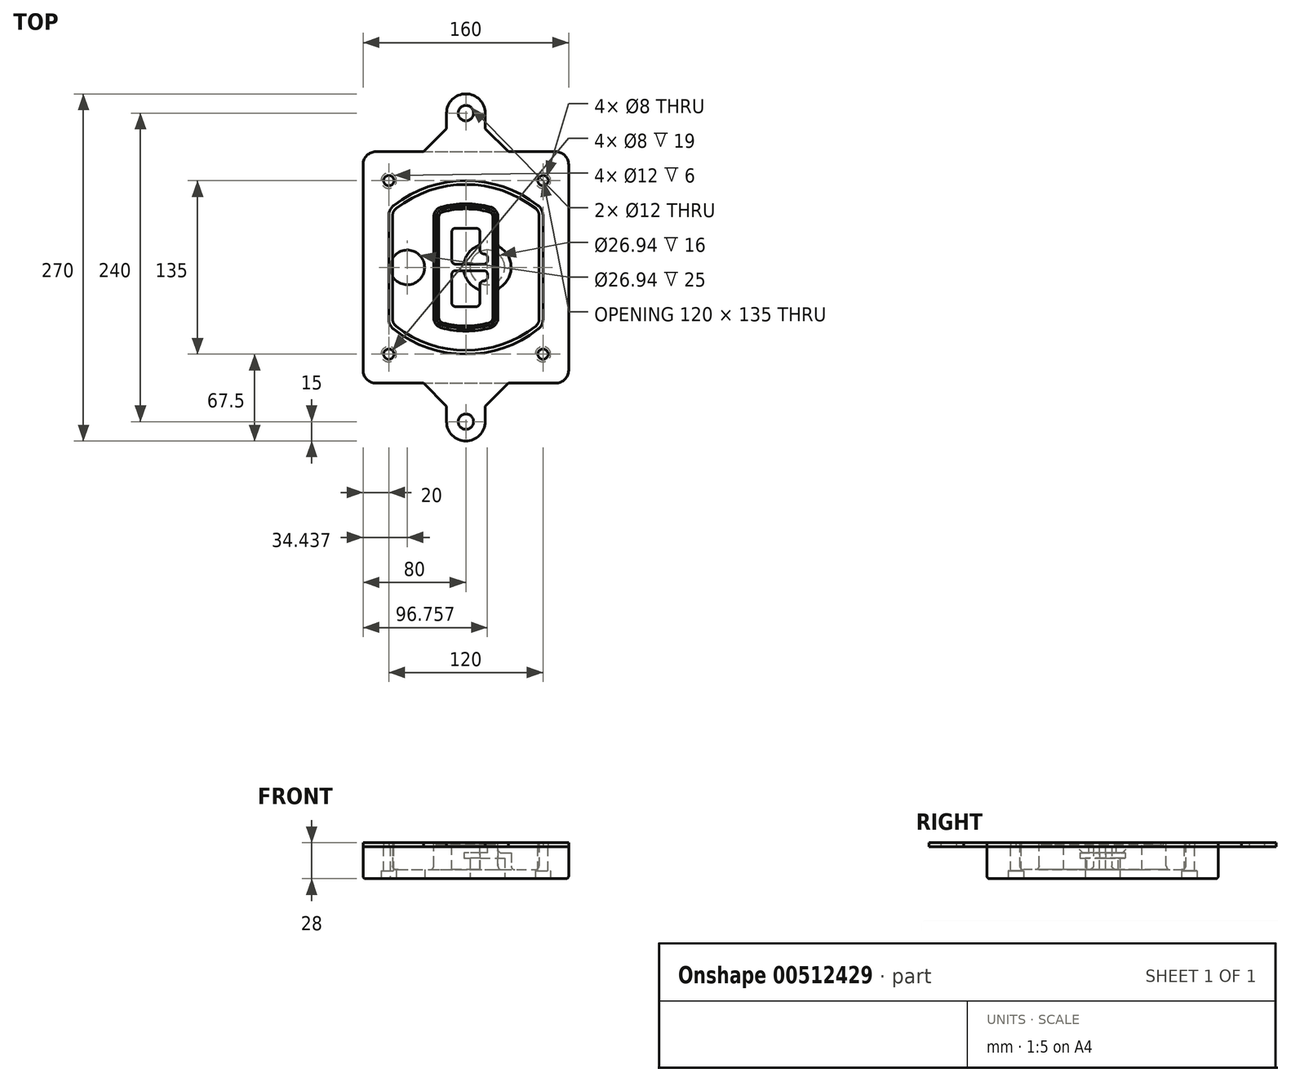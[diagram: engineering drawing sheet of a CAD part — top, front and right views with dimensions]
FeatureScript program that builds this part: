
annotation { "Feature Type Name" : "Feature", "Feature Type Description" : "" }
export const myFeature = defineFeature(function(context is Context, id is Id, definition is map)
    precondition{}
    {
        {
            var Q0;
            Q0=qCreatedBy(makeId("Top.planeOp"),FACE);
            var sketch = newSketch(context, id + "F0", { "sketchPlane" : qUnion([Q0])});
            skPoint(sketch, "E0.rect.middle", {"position": v(0, 0) * mm});
            skLineSegment(sketch, "E1.bottom", {"start": v(-70, -90) * mm, "end": v(70, -90) * mm});
            skLineSegment(sketch, "E1.top", {"start": v(-70, 90) * mm, "end": v(70, 90) * mm});
            skLineSegment(sketch, "E1.left", {"start": v(-80, -80) * mm, "end": v(-80, 80) * mm});
            skLineSegment(sketch, "E1.right", {"start": v(80, -80) * mm, "end": v(80, 80) * mm});
            skLineSegment(sketch, "E2", {"start": v(-80, 90) * mm, "end": v(80, -90) * mm, "construction": true});
            skLineSegment(sketch, "E3", {"start": v(80, 90) * mm, "end": v(-80, -90) * mm, "construction": true});
            skCircle(sketch, "E4", {"center": v(-60, 67.5) * mm, "radius": 4 * mm});
            skCircle(sketch, "E5", {"center": v(60, 67.5) * mm, "radius": 4 * mm});
            skCircle(sketch, "E6", {"center": v(60, -67.5) * mm, "radius": 4 * mm});
            skCircle(sketch, "E7", {"center": v(-60, -67.5) * mm, "radius": 4 * mm});
            skLineSegment(sketch, "E8", {"start": v(-60, 67.5) * mm, "end": v(60, 67.5) * mm, "construction": true});
            skLineSegment(sketch, "E9", {"start": v(60, 67.5) * mm, "end": v(60, -67.5) * mm, "construction": true});
            skLineSegment(sketch, "E10", {"start": v(60, -67.5) * mm, "end": v(-60, -67.5) * mm, "construction": true});
            skLineSegment(sketch, "E11", {"start": v(-60, -67.5) * mm, "end": v(-60, 67.5) * mm, "construction": true});
            skLineSegment(sketch, "E12", {"start": v(-60, 40.3) * mm, "end": v(-60, -40.3) * mm});
            skLineSegment(sketch, "E13", {"start": v(60, 40.3) * mm, "end": v(60, -40.3) * mm});
            skArc(sketch, "E14", {"start": v(56.15, 48.18) * mm, "mid": v(0, 67.5) * mm, "end": v(-56.15, 48.18) * mm});
            skArc(sketch, "E15", {"start": v(-56.15, -48.18) * mm, "mid": v(0, -67.5) * mm, "end": v(56.15, -48.18) * mm});
            skLineSegment(sketch, "E16", {"start": v(-60, 0) * mm, "end": v(60, 0) * mm, "construction": true});
            skPoint(sketch, "E17.visualSharp", {"position": v(-60, -45) * mm});
            skArc(sketch, "E17.filletArc", {"start": v(-60, -40.3) * mm, "mid": v(-58.99, -44.68) * mm, "end": v(-56.15, -48.18) * mm});
            skPoint(sketch, "E18.visualSharp", {"position": v(-60, 45) * mm});
            skArc(sketch, "E18.filletArc", {"start": v(-56.15, 48.18) * mm, "mid": v(-58.99, 44.68) * mm, "end": v(-60, 40.3) * mm});
            skPoint(sketch, "E19.visualSharp", {"position": v(60, 45) * mm});
            skArc(sketch, "E19.filletArc", {"start": v(60, 40.3) * mm, "mid": v(58.99, 44.68) * mm, "end": v(56.15, 48.18) * mm});
            skPoint(sketch, "E20.visualSharp", {"position": v(60, -45) * mm});
            skArc(sketch, "E20.filletArc", {"start": v(56.15, -48.18) * mm, "mid": v(58.99, -44.68) * mm, "end": v(60, -40.3) * mm});
            skPoint(sketch, "E21.visualSharp", {"position": v(-80, 90) * mm});
            skArc(sketch, "E21.filletArc", {"start": v(-70, 90) * mm, "mid": v(-77.07, 87.07) * mm, "end": v(-80, 80) * mm});
            skPoint(sketch, "E22.visualSharp", {"position": v(80, 90) * mm});
            skArc(sketch, "E22.filletArc", {"start": v(80, 80) * mm, "mid": v(77.07, 87.07) * mm, "end": v(70, 90) * mm});
            skPoint(sketch, "E23.visualSharp", {"position": v(80, -90) * mm});
            skArc(sketch, "E23.filletArc", {"start": v(70, -90) * mm, "mid": v(77.07, -87.07) * mm, "end": v(80, -80) * mm});
            skPoint(sketch, "E24.visualSharp", {"position": v(-80, -90) * mm});
            skArc(sketch, "E24.filletArc", {"start": v(-80, -80) * mm, "mid": v(-77.07, -87.07) * mm, "end": v(-70, -90) * mm});
            skArc(sketch, "E25.0", {"start": v(57, 40.3) * mm, "mid": v(56.3, 43.36) * mm, "end": v(54.3, 45.81) * mm});
            skLineSegment(sketch, "E25.1", {"start": v(57, 40.3) * mm, "end": v(57, -40.3) * mm});
            skArc(sketch, "E25.2", {"start": v(54.3, -45.81) * mm, "mid": v(56.3, -43.36) * mm, "end": v(57, -40.3) * mm});
            skArc(sketch, "E25.3", {"start": v(-54.3, -45.81) * mm, "mid": v(0, -64.5) * mm, "end": v(54.3, -45.81) * mm});
            skArc(sketch, "E25.4", {"start": v(-57, -40.3) * mm, "mid": v(-56.3, -43.36) * mm, "end": v(-54.3, -45.81) * mm});
            skArc(sketch, "E25.5", {"start": v(54.3, 45.81) * mm, "mid": v(0, 64.5) * mm, "end": v(-54.3, 45.81) * mm});
            skLineSegment(sketch, "E25.6", {"start": v(-57, 40.3) * mm, "end": v(-57, -40.3) * mm});
            skArc(sketch, "E25.7", {"start": v(-54.3, 45.81) * mm, "mid": v(-56.3, 43.36) * mm, "end": v(-57, 40.3) * mm});
            skArc(sketch, "E26.0", {"start": v(-58.62, 51.33) * mm, "mid": v(-62.58, 46.43) * mm, "end": v(-64, 40.3) * mm});
            skArc(sketch, "E26.1", {"start": v(58.62, 51.33) * mm, "mid": v(0, 71.5) * mm, "end": v(-58.62, 51.33) * mm});
            skArc(sketch, "E26.2", {"start": v(64, 40.3) * mm, "mid": v(62.58, 46.43) * mm, "end": v(58.62, 51.33) * mm});
            skLineSegment(sketch, "E26.3", {"start": v(64, 40.3) * mm, "end": v(64, -40.3) * mm});
            skArc(sketch, "E26.4", {"start": v(58.62, -51.33) * mm, "mid": v(62.58, -46.43) * mm, "end": v(64, -40.3) * mm});
            skLineSegment(sketch, "E26.5", {"start": v(-64, 40.3) * mm, "end": v(-64, -40.3) * mm});
            skArc(sketch, "E26.6", {"start": v(-58.62, -51.33) * mm, "mid": v(0, -71.5) * mm, "end": v(58.62, -51.33) * mm});
            skArc(sketch, "E26.7", {"start": v(-64, -40.3) * mm, "mid": v(-62.58, -46.43) * mm, "end": v(-58.62, -51.33) * mm});
            skSolve(sketch);
        }
        {
            var Q0;
            Q0=makeQuery(id+"F0.imprint","IMPRINT",FACE,{"disambiguationData":[TD([[makeQuery(id+"F0.imprint","IMPRINT",EDGE,{"derivedFrom":sQuery(id+"F0.wireOp",EDGE,"E1.bottom")}),1.0]])]});
            var Q1;
            Q1=makeQuery(id+"F0.imprint","IMPRINT",FACE,{"disambiguationData":[TD([[makeQuery(id+"F0.imprint","IMPRINT",EDGE,{"derivedFrom":sQuery(id+"F0.wireOp",EDGE,"E12")}),1.0]])]});
            var Q2;
            Q2=makeQuery(id+"F0.imprint","IMPRINT",FACE,{"disambiguationData":[TD([[makeQuery(id+"F0.imprint","IMPRINT",EDGE,{"derivedFrom":sQuery(id+"F0.wireOp",EDGE,"E25.0")}),1.0]])]});
            var Q3;
            Q3=makeQuery(id+"F0.imprint","IMPRINT",FACE,{"disambiguationData":[TD([[makeQuery(id+"F0.imprint","IMPRINT",EDGE,{"derivedFrom":sQuery(id+"F0.wireOp",EDGE,"E12")}),-1.0]])]});
            extrude(context, id + "F1", {"entities" : qUnion([Q0, Q1, Q2, Q3]), "oppositeDirection" : true, "depth" : 25 * mm});
        }
        {
            var Q0;
            Q0=makeQuery(id+"F0.imprint","IMPRINT",FACE,{"disambiguationData":[TD([[makeQuery(id+"F0.imprint","IMPRINT",EDGE,{"derivedFrom":sQuery(id+"F0.wireOp",EDGE,"E12")}),1.0]])]});
            extrude(context, id + "F2", {"entities" : qUnion([Q0]), "operationType" : NewBodyOperationType.ADD, "depth" : 3 * mm});
        }
        {
            var Q0;
            Q0=makeQuery(id+"F0.imprint","IMPRINT",FACE,{"disambiguationData":[TD([[makeQuery(id+"F0.imprint","IMPRINT",EDGE,{"derivedFrom":sQuery(id+"F0.wireOp",EDGE,"E25.0")}),1.0]])]});
            extrude(context, id + "F3", {"entities" : qUnion([Q0]), "operationType" : NewBodyOperationType.REMOVE, "oppositeDirection" : true, "depth" : 18 * mm});
        }
        {
            var Q0;
            Q0=makeQuery(id+"F2.opExtrude","CAP_FACE",FACE,{"disambiguationData":[OSD([sQuery(id+"F0.wireOp",EDGE,"E12"),sQuery(id+"F0.wireOp",EDGE,"E13"),sQuery(id+"F0.wireOp",EDGE,"E14"),sQuery(id+"F0.wireOp",EDGE,"E15"),sQuery(id+"F0.wireOp",EDGE,"E17.filletArc"),sQuery(id+"F0.wireOp",EDGE,"E18.filletArc"),sQuery(id+"F0.wireOp",EDGE,"E19.filletArc"),sQuery(id+"F0.wireOp",EDGE,"E20.filletArc"),sQuery(id+"F0.wireOp",EDGE,"E25.0"),sQuery(id+"F0.wireOp",EDGE,"E25.1"),sQuery(id+"F0.wireOp",EDGE,"E25.2"),sQuery(id+"F0.wireOp",EDGE,"E25.3"),sQuery(id+"F0.wireOp",EDGE,"E25.4"),sQuery(id+"F0.wireOp",EDGE,"E25.5"),sQuery(id+"F0.wireOp",EDGE,"E25.6"),sQuery(id+"F0.wireOp",EDGE,"E25.7")])],"isStart":false});
            var sketch = newSketch(context, id + "F4", { "sketchPlane" : qUnion([Q0])});
            skArc(sketch, "E27.0", {"start": v(-19.08, -46.97) * mm, "mid": v(0, -49.5) * mm, "end": v(19.08, -46.97) * mm});
            skArc(sketch, "E28.0", {"start": v(19.08, 46.97) * mm, "mid": v(0, 49.5) * mm, "end": v(-19.08, 46.97) * mm});
            skLineSegment(sketch, "E29", {"start": v(-25, 39.25) * mm, "end": v(-25, -39.25) * mm});
            skLineSegment(sketch, "E30", {"start": v(25, 39.25) * mm, "end": v(25, -39.25) * mm});
            skLineSegment(sketch, "E31", {"start": v(-25, 45.1) * mm, "end": v(25, 45.1) * mm, "construction": true});
            skLineSegment(sketch, "E32", {"start": v(-25, -45.1) * mm, "end": v(25, -45.1) * mm, "construction": true});
            skPoint(sketch, "E33.visualSharp", {"position": v(-25, 45.1) * mm});
            skArc(sketch, "E33.filletArc", {"start": v(-19.08, 46.97) * mm, "mid": v(-23.35, 44.11) * mm, "end": v(-25, 39.25) * mm});
            skPoint(sketch, "E34.visualSharp", {"position": v(25, 45.1) * mm});
            skArc(sketch, "E34.filletArc", {"start": v(25, 39.25) * mm, "mid": v(23.35, 44.11) * mm, "end": v(19.08, 46.97) * mm});
            skPoint(sketch, "E35.visualSharp", {"position": v(25, -45.1) * mm});
            skArc(sketch, "E35.filletArc", {"start": v(19.08, -46.97) * mm, "mid": v(23.35, -44.11) * mm, "end": v(25, -39.25) * mm});
            skPoint(sketch, "E36.visualSharp", {"position": v(-25, -45.1) * mm});
            skArc(sketch, "E36.filletArc", {"start": v(-25, -39.25) * mm, "mid": v(-23.35, -44.11) * mm, "end": v(-19.08, -46.97) * mm});
            skArc(sketch, "E37.0", {"start": v(54.3, 45.81) * mm, "mid": v(0, 64.5) * mm, "end": v(-54.3, 45.81) * mm});
            skArc(sketch, "E37.1", {"start": v(-54.3, 45.81) * mm, "mid": v(-56.3, 43.36) * mm, "end": v(-57, 40.3) * mm});
            skLineSegment(sketch, "E37.2", {"start": v(-57, 40.3) * mm, "end": v(-57, -40.3) * mm});
            skArc(sketch, "E37.3", {"start": v(-57, -40.3) * mm, "mid": v(-56.3, -43.36) * mm, "end": v(-54.3, -45.81) * mm});
            skArc(sketch, "E37.4", {"start": v(-54.3, -45.81) * mm, "mid": v(0, -64.5) * mm, "end": v(54.3, -45.81) * mm});
            skArc(sketch, "E37.5", {"start": v(54.3, -45.81) * mm, "mid": v(56.3, -43.36) * mm, "end": v(57, -40.3) * mm});
            skLineSegment(sketch, "E37.6", {"start": v(57, 40.3) * mm, "end": v(57, -40.3) * mm});
            skArc(sketch, "E37.7", {"start": v(57, 40.3) * mm, "mid": v(56.3, 43.36) * mm, "end": v(54.3, 45.81) * mm});
            skLineSegment(sketch, "E38.0", {"start": v(23, 39.25) * mm, "end": v(23, -39.25) * mm});
            skArc(sketch, "E38.1", {"start": v(18.56, -45.04) * mm, "mid": v(21.76, -42.9) * mm, "end": v(23, -39.25) * mm});
            skArc(sketch, "E38.2", {"start": v(-18.56, -45.04) * mm, "mid": v(0, -47.5) * mm, "end": v(18.56, -45.04) * mm});
            skArc(sketch, "E38.3", {"start": v(-23, -39.25) * mm, "mid": v(-21.76, -42.9) * mm, "end": v(-18.56, -45.04) * mm});
            skLineSegment(sketch, "E38.4", {"start": v(-23, 39.25) * mm, "end": v(-23, -39.25) * mm});
            skArc(sketch, "E38.5", {"start": v(23, 39.25) * mm, "mid": v(21.76, 42.9) * mm, "end": v(18.56, 45.04) * mm});
            skArc(sketch, "E38.6", {"start": v(-18.56, 45.04) * mm, "mid": v(-21.76, 42.9) * mm, "end": v(-23, 39.25) * mm});
            skArc(sketch, "E38.7", {"start": v(18.56, 45.04) * mm, "mid": v(0, 47.5) * mm, "end": v(-18.56, 45.04) * mm});
            skArc(sketch, "E39.0", {"start": v(21, 39.25) * mm, "mid": v(20.18, 41.68) * mm, "end": v(18.04, 43.1) * mm});
            skLineSegment(sketch, "E39.1", {"start": v(21, 39.25) * mm, "end": v(21, -39.25) * mm});
            skArc(sketch, "E39.2", {"start": v(18.04, -43.1) * mm, "mid": v(20.18, -41.68) * mm, "end": v(21, -39.25) * mm});
            skArc(sketch, "E39.3", {"start": v(-18.04, -43.1) * mm, "mid": v(0, -45.5) * mm, "end": v(18.04, -43.1) * mm});
            skArc(sketch, "E39.4", {"start": v(-21, -39.25) * mm, "mid": v(-20.18, -41.68) * mm, "end": v(-18.04, -43.1) * mm});
            skArc(sketch, "E39.5", {"start": v(18.04, 43.1) * mm, "mid": v(0, 45.5) * mm, "end": v(-18.04, 43.1) * mm});
            skLineSegment(sketch, "E39.6", {"start": v(-21, 39.25) * mm, "end": v(-21, -39.25) * mm});
            skArc(sketch, "E39.7", {"start": v(-18.04, 43.1) * mm, "mid": v(-20.18, 41.68) * mm, "end": v(-21, 39.25) * mm});
            skLineSegment(sketch, "E40", {"start": v(-25, 0) * mm, "end": v(25, 0) * mm, "construction": true});
            skLineSegment(sketch, "E41", {"start": v(-11, 5.5) * mm, "end": v(-11, 27.5) * mm});
            skLineSegment(sketch, "E42", {"start": v(-8, 30.5) * mm, "end": v(8, 30.5) * mm});
            skLineSegment(sketch, "E43", {"start": v(11, 27.5) * mm, "end": v(11, 13.5) * mm});
            skLineSegment(sketch, "E44", {"start": v(14, 10.5) * mm, "end": v(14, 10.5) * mm});
            skLineSegment(sketch, "E45", {"start": v(17, 7.5) * mm, "end": v(17, 5.5) * mm});
            skLineSegment(sketch, "E46", {"start": v(14, 2.5) * mm, "end": v(-8, 2.5) * mm});
            skPoint(sketch, "E47.visualSharp", {"position": v(-11, 30.5) * mm});
            skArc(sketch, "E47.filletArc", {"start": v(-8, 30.5) * mm, "mid": v(-10.12, 29.62) * mm, "end": v(-11, 27.5) * mm});
            skPoint(sketch, "E48.visualSharp", {"position": v(11, 30.5) * mm});
            skArc(sketch, "E48.filletArc", {"start": v(11, 27.5) * mm, "mid": v(10.12, 29.62) * mm, "end": v(8, 30.5) * mm});
            skPoint(sketch, "E49.visualSharp", {"position": v(11, 10.5) * mm});
            skArc(sketch, "E49.filletArc", {"start": v(11, 13.5) * mm, "mid": v(11.88, 11.38) * mm, "end": v(14, 10.5) * mm});
            skPoint(sketch, "E50.visualSharp", {"position": v(17, 10.5) * mm});
            skArc(sketch, "E50.filletArc", {"start": v(17, 7.5) * mm, "mid": v(16.12, 9.62) * mm, "end": v(14, 10.5) * mm});
            skPoint(sketch, "E51.visualSharp", {"position": v(17, 2.5) * mm});
            skArc(sketch, "E51.filletArc", {"start": v(14, 2.5) * mm, "mid": v(16.12, 3.38) * mm, "end": v(17, 5.5) * mm});
            skPoint(sketch, "E52.visualSharp", {"position": v(-11, 2.5) * mm});
            skArc(sketch, "E52.filletArc", {"start": v(-11, 5.5) * mm, "mid": v(-10.12, 3.38) * mm, "end": v(-8, 2.5) * mm});
            skLineSegment(sketch, "E53.0.MirrorCS", {"start": v(14, -2.5) * mm, "end": v(-8, -2.5) * mm});
            skArc(sketch, "E54.0.MirrorCS", {"start": v(-11, -5.5) * mm, "mid": v(-10.12, -3.38) * mm, "end": v(-8, -2.5) * mm});
            skLineSegment(sketch, "E55.0.MirrorCS", {"start": v(-11, -5.5) * mm, "end": v(-11, -27.5) * mm});
            skArc(sketch, "E56.0.MirrorCS", {"start": v(-8, -30.5) * mm, "mid": v(-10.12, -29.62) * mm, "end": v(-11, -27.5) * mm});
            skLineSegment(sketch, "E57.0.MirrorCS", {"start": v(-8, -30.5) * mm, "end": v(8, -30.5) * mm});
            skArc(sketch, "E58.0.MirrorCS", {"start": v(11, -27.5) * mm, "mid": v(10.12, -29.62) * mm, "end": v(8, -30.5) * mm});
            skLineSegment(sketch, "E59.0.MirrorCS", {"start": v(11, -27.5) * mm, "end": v(11, -13.5) * mm});
            skArc(sketch, "E60.0.MirrorCS", {"start": v(11, -13.5) * mm, "mid": v(11.88, -11.38) * mm, "end": v(14, -10.5) * mm});
            skArc(sketch, "E61.0.MirrorCS", {"start": v(17, -7.5) * mm, "mid": v(16.12, -9.62) * mm, "end": v(14, -10.5) * mm});
            skLineSegment(sketch, "E62.0.MirrorCS", {"start": v(17, -7.5) * mm, "end": v(17, -5.5) * mm});
            skArc(sketch, "E63.0.MirrorCS", {"start": v(14, -2.5) * mm, "mid": v(16.12, -3.38) * mm, "end": v(17, -5.5) * mm});
            skSolve(sketch);
        }
        {
            var Q0;
            Q0=makeQuery(id+"F4.imprint","IMPRINT",FACE,{"disambiguationData":[TD([[makeQuery(id+"F4.imprint","IMPRINT",EDGE,{"derivedFrom":sQuery(id+"F4.wireOp",EDGE,"E27.0")}),1.0]])]});
            var Q1;
            Q1=makeQuery(id+"F4.imprint","IMPRINT",FACE,{"disambiguationData":[TD([[makeQuery(id+"F4.imprint","IMPRINT",EDGE,{"derivedFrom":sQuery(id+"F4.wireOp",EDGE,"E38.0")}),-1.0]])]});
            var Q2;
            Q2=makeQuery(id+"F4.imprint","IMPRINT",FACE,{"disambiguationData":[TD([[makeQuery(id+"F4.imprint","IMPRINT",EDGE,{"derivedFrom":sQuery(id+"F4.wireOp",EDGE,"E39.0")}),1.0]])]});
            extrude(context, id + "F5", {"entities" : qUnion([Q0, Q1, Q2]), "operationType" : NewBodyOperationType.ADD, "endBound" : BoundingType.UP_TO_NEXT, "oppositeDirection" : true, "depth" : 25 * mm});
        }
        {
            var Q0;
            Q0=makeQuery(id+"F4.imprint","IMPRINT",FACE,{"disambiguationData":[TD([[makeQuery(id+"F4.imprint","IMPRINT",EDGE,{"derivedFrom":sQuery(id+"F4.wireOp",EDGE,"E38.0")}),-1.0]])]});
            extrude(context, id + "F6", {"entities" : qUnion([Q0]), "operationType" : NewBodyOperationType.REMOVE, "oppositeDirection" : true, "depth" : 2 * mm});
        }
        {
            var Q0;
            Q0=makeQuery(id+"F1.opExtrude","CAP_FACE",FACE,{"disambiguationData":[OSD([sQuery(id+"F0.wireOp",EDGE,"E1.bottom"),sQuery(id+"F0.wireOp",EDGE,"E1.top"),sQuery(id+"F0.wireOp",EDGE,"E1.left"),sQuery(id+"F0.wireOp",EDGE,"E1.right"),sQuery(id+"F0.wireOp",EDGE,"E4"),sQuery(id+"F0.wireOp",EDGE,"E5"),sQuery(id+"F0.wireOp",EDGE,"E6"),sQuery(id+"F0.wireOp",EDGE,"E7"),sQuery(id+"F0.wireOp",EDGE,"E21.filletArc"),sQuery(id+"F0.wireOp",EDGE,"E22.filletArc"),sQuery(id+"F0.wireOp",EDGE,"E23.filletArc"),sQuery(id+"F0.wireOp",EDGE,"E24.filletArc")])],"isStart":false});
            var sketch = newSketch(context, id + "F7", { "sketchPlane" : qUnion([Q0])});
            skCircle(sketch, "E64", {"center": v(16.76, 0) * mm, "radius": 13.47 * mm});
            skCircle(sketch, "E65", {"center": v(-45.56, 0) * mm, "radius": 13.47 * mm});
            skLineSegment(sketch, "E66", {"start": v(80, 0) * mm, "end": v(-80, 0) * mm});
            skCircle(sketch, "E67", {"center": v(16.76, 0) * mm, "radius": 18.47 * mm});
            skCircle(sketch, "E68", {"center": v(60, -67.5) * mm, "radius": 6 * mm});
            skCircle(sketch, "E69", {"center": v(-60, -67.5) * mm, "radius": 6 * mm});
            skCircle(sketch, "E70", {"center": v(-60, 67.5) * mm, "radius": 6 * mm});
            skCircle(sketch, "E71", {"center": v(60, 67.5) * mm, "radius": 6 * mm});
            skSolve(sketch);
        }
        {
            var Q0;
            {var subQ1=sQuery(id+"F7.wireOp",EDGE,"E66");var subQ4=sQuery(id+"F7.wireOp",EDGE,"E64");var subQ6=makeQuery(id+"F7.imprint","INTERSECT",VERTEX,{"disambiguationData":[OD(0.0)],"derivedFrom":[subQ4,subQ1]});Q0=makeQuery(id+"F7.imprint","IMPRINT",FACE,{"disambiguationData":[TD([[makeQuery(id+"F7.imprint","IMPRINT",EDGE,{"disambiguationData":[TD([[subQ6,-1.0]])],"derivedFrom":subQ4}),-1.0]])]});}
            var Q1;
            {var subQ0=sQuery(id+"F7.wireOp",EDGE,"E66");var subQ1=sQuery(id+"F7.wireOp",EDGE,"E64");var subQ3=makeQuery(id+"F7.imprint","INTERSECT",VERTEX,{"disambiguationData":[OD(0.0)],"derivedFrom":[subQ1,subQ0]});Q1=makeQuery(id+"F7.imprint","IMPRINT",FACE,{"disambiguationData":[TD([[makeQuery(id+"F7.imprint","IMPRINT",EDGE,{"disambiguationData":[TD([[subQ3,-1.0]])],"derivedFrom":subQ1}),1.0]])]});}
            var Q2;
            {var subQ0=sQuery(id+"F7.wireOp",EDGE,"E66");var subQ1=sQuery(id+"F7.wireOp",EDGE,"E64");var subQ3=makeQuery(id+"F7.imprint","INTERSECT",VERTEX,{"disambiguationData":[OD(0.0)],"derivedFrom":[subQ1,subQ0]});Q2=makeQuery(id+"F7.imprint","IMPRINT",FACE,{"disambiguationData":[TD([[makeQuery(id+"F7.imprint","IMPRINT",EDGE,{"disambiguationData":[TD([[subQ3,1.0]])],"derivedFrom":subQ1}),1.0]])]});}
            var Q3;
            {var subQ1=sQuery(id+"F7.wireOp",EDGE,"E66");var subQ4=sQuery(id+"F7.wireOp",EDGE,"E64");var subQ6=makeQuery(id+"F7.imprint","INTERSECT",VERTEX,{"disambiguationData":[OD(0.0)],"derivedFrom":[subQ4,subQ1]});Q3=makeQuery(id+"F7.imprint","IMPRINT",FACE,{"disambiguationData":[TD([[makeQuery(id+"F7.imprint","IMPRINT",EDGE,{"disambiguationData":[TD([[subQ6,1.0]])],"derivedFrom":subQ4}),-1.0]])]});}
            extrude(context, id + "F8", {"entities" : qUnion([Q0, Q1, Q2, Q3]), "operationType" : NewBodyOperationType.ADD, "oppositeDirection" : true, "depth" : 20 * mm});
        }
        {
            var Q0;
            {var subQ0=sQuery(id+"F7.wireOp",EDGE,"E66");var subQ1=sQuery(id+"F7.wireOp",EDGE,"E64");var subQ3=makeQuery(id+"F7.imprint","INTERSECT",VERTEX,{"disambiguationData":[OD(0.0)],"derivedFrom":[subQ1,subQ0]});Q0=makeQuery(id+"F7.imprint","IMPRINT",FACE,{"disambiguationData":[TD([[makeQuery(id+"F7.imprint","IMPRINT",EDGE,{"disambiguationData":[TD([[subQ3,-1.0]])],"derivedFrom":subQ1}),1.0]])]});}
            var Q1;
            {var subQ0=sQuery(id+"F7.wireOp",EDGE,"E66");var subQ1=sQuery(id+"F7.wireOp",EDGE,"E64");var subQ3=makeQuery(id+"F7.imprint","INTERSECT",VERTEX,{"disambiguationData":[OD(0.0)],"derivedFrom":[subQ1,subQ0]});Q1=makeQuery(id+"F7.imprint","IMPRINT",FACE,{"disambiguationData":[TD([[makeQuery(id+"F7.imprint","IMPRINT",EDGE,{"disambiguationData":[TD([[subQ3,1.0]])],"derivedFrom":subQ1}),1.0]])]});}
            extrude(context, id + "F9", {"entities" : qUnion([Q0, Q1]), "operationType" : NewBodyOperationType.REMOVE, "oppositeDirection" : true, "depth" : 16 * mm});
        }
        {
            var Q0;
            {var subQ0=sQuery(id+"F7.wireOp",EDGE,"E66");var subQ1=sQuery(id+"F7.wireOp",EDGE,"E65");var subQ3=makeQuery(id+"F7.imprint","INTERSECT",VERTEX,{"disambiguationData":[OD(0.0)],"derivedFrom":[subQ1,subQ0]});Q0=makeQuery(id+"F7.imprint","IMPRINT",FACE,{"disambiguationData":[TD([[makeQuery(id+"F7.imprint","IMPRINT",EDGE,{"disambiguationData":[TD([[subQ3,-1.0]])],"derivedFrom":subQ1}),1.0]])]});}
            var Q1;
            {var subQ0=sQuery(id+"F7.wireOp",EDGE,"E66");var subQ1=sQuery(id+"F7.wireOp",EDGE,"E65");var subQ3=makeQuery(id+"F7.imprint","INTERSECT",VERTEX,{"disambiguationData":[OD(0.0)],"derivedFrom":[subQ1,subQ0]});Q1=makeQuery(id+"F7.imprint","IMPRINT",FACE,{"disambiguationData":[TD([[makeQuery(id+"F7.imprint","IMPRINT",EDGE,{"disambiguationData":[TD([[subQ3,1.0]])],"derivedFrom":subQ1}),1.0]])]});}
            extrude(context, id + "F10", {"entities" : qUnion([Q0, Q1]), "operationType" : NewBodyOperationType.REMOVE, "oppositeDirection" : true, "depth" : 25 * mm});
        }
        {
            var Q0;
            Q0=makeQuery(id+"F7.imprint","IMPRINT",FACE,{"disambiguationData":[TD([[makeQuery(id+"F7.imprint","IMPRINT",EDGE,{"derivedFrom":sQuery(id+"F7.wireOp",EDGE,"E68")}),1.0]])]});
            var Q1;
            Q1=makeQuery(id+"F7.imprint","IMPRINT",FACE,{"disambiguationData":[TD([[makeQuery(id+"F7.imprint","IMPRINT",EDGE,{"derivedFrom":makeQuery(id+"F1.opExtrude","CAP_EDGE",EDGE,{"disambiguationData":[OSD([sQuery(id+"F0.wireOp",EDGE,"E5")])],"isStart":false})}),-1.0]])]});
            var Q2;
            Q2=makeQuery(id+"F7.imprint","IMPRINT",FACE,{"disambiguationData":[TD([[makeQuery(id+"F7.imprint","IMPRINT",EDGE,{"derivedFrom":sQuery(id+"F7.wireOp",EDGE,"E69")}),1.0]])]});
            var Q3;
            Q3=makeQuery(id+"F7.imprint","IMPRINT",FACE,{"disambiguationData":[TD([[makeQuery(id+"F7.imprint","IMPRINT",EDGE,{"derivedFrom":makeQuery(id+"F1.opExtrude","CAP_EDGE",EDGE,{"disambiguationData":[OSD([sQuery(id+"F0.wireOp",EDGE,"E4")])],"isStart":false})}),-1.0]])]});
            var Q4;
            Q4=makeQuery(id+"F7.imprint","IMPRINT",FACE,{"disambiguationData":[TD([[makeQuery(id+"F7.imprint","IMPRINT",EDGE,{"derivedFrom":sQuery(id+"F7.wireOp",EDGE,"E70")}),1.0]])]});
            var Q5;
            Q5=makeQuery(id+"F7.imprint","IMPRINT",FACE,{"disambiguationData":[TD([[makeQuery(id+"F7.imprint","IMPRINT",EDGE,{"derivedFrom":makeQuery(id+"F1.opExtrude","CAP_EDGE",EDGE,{"disambiguationData":[OSD([sQuery(id+"F0.wireOp",EDGE,"E7")])],"isStart":false})}),-1.0]])]});
            var Q6;
            Q6=makeQuery(id+"F7.imprint","IMPRINT",FACE,{"disambiguationData":[TD([[makeQuery(id+"F7.imprint","IMPRINT",EDGE,{"derivedFrom":sQuery(id+"F7.wireOp",EDGE,"E71")}),1.0]])]});
            var Q7;
            Q7=makeQuery(id+"F7.imprint","IMPRINT",FACE,{"disambiguationData":[TD([[makeQuery(id+"F7.imprint","IMPRINT",EDGE,{"derivedFrom":makeQuery(id+"F1.opExtrude","CAP_EDGE",EDGE,{"disambiguationData":[OSD([sQuery(id+"F0.wireOp",EDGE,"E6")])],"isStart":false})}),-1.0]])]});
            extrude(context, id + "F11", {"entities" : qUnion([Q0, Q1, Q2, Q3, Q4, Q5, Q6, Q7]), "operationType" : NewBodyOperationType.REMOVE, "oppositeDirection" : true, "depth" : 6 * mm});
        }
        {
            var Q0;
            Q0=makeQuery(id+"F9.boolean.opBoolean","COPY",FACE,{"derivedFrom":makeQuery(id+"F9.opExtrude","CAP_FACE",FACE,{"disambiguationData":[OSD([sQuery(id+"F7.wireOp",EDGE,"E64")])],"isStart":false})});
            var sketch = newSketch(context, id + "F12", { "sketchPlane" : qUnion([Q0])});
            skArc(sketch, "E72.0", {"start": v(11, 17.55) * mm, "mid": v(2.57, 11.82) * mm, "end": v(-1.54, 2.5) * mm});
            skArc(sketch, "E72.1", {"start": v(-1.54, -2.5) * mm, "mid": v(2.57, -11.82) * mm, "end": v(11, -17.55) * mm});
            skLineSegment(sketch, "E73", {"start": v(-1.54, -2.5) * mm, "end": v(14, -2.5) * mm});
            skLineSegment(sketch, "E74.0", {"start": v(14, 2.5) * mm, "end": v(-1.54, 2.5) * mm});
            skArc(sketch, "E74.1", {"start": v(14, 2.5) * mm, "mid": v(16.12, 3.38) * mm, "end": v(17, 5.5) * mm});
            skLineSegment(sketch, "E74.2", {"start": v(17, 7.5) * mm, "end": v(17, 5.5) * mm});
            skArc(sketch, "E74.3", {"start": v(17, 7.5) * mm, "mid": v(16.12, 9.62) * mm, "end": v(14, 10.5) * mm});
            skArc(sketch, "E74.4", {"start": v(11, 13.5) * mm, "mid": v(11.88, 11.38) * mm, "end": v(14, 10.5) * mm});
            skLineSegment(sketch, "E74.5", {"start": v(11, 17.55) * mm, "end": v(11, 13.5) * mm});
            skLineSegment(sketch, "E74.7", {"start": v(14, -2.5) * mm, "end": v(-1.54, -2.5) * mm});
            skArc(sketch, "E74.8", {"start": v(14, -2.5) * mm, "mid": v(16.12, -3.38) * mm, "end": v(17, -5.5) * mm});
            skLineSegment(sketch, "E74.9", {"start": v(17, -7.5) * mm, "end": v(17, -5.5) * mm});
            skArc(sketch, "E74.10", {"start": v(17, -7.5) * mm, "mid": v(16.12, -9.62) * mm, "end": v(14, -10.5) * mm});
            skArc(sketch, "E74.11", {"start": v(11, -13.5) * mm, "mid": v(11.88, -11.38) * mm, "end": v(14, -10.5) * mm});
            skLineSegment(sketch, "E74.12", {"start": v(11, -17.55) * mm, "end": v(11, -13.5) * mm});
            skPoint(sketch, "E75.orphan", {"position": v(11, -27.5) * mm});
            skPoint(sketch, "E76.orphan", {"position": v(-8, -2.5) * mm});
            skPoint(sketch, "E77.orphan", {"position": v(-8, 2.5) * mm});
            skPoint(sketch, "E78.orphan", {"position": v(11, 27.5) * mm});
            skSolve(sketch);
        }
        {
            var Q0;
            {var subQ7=sQuery(id+"F12.wireOp",EDGE,"E72.0");var subQ14=sQuery(id+"F12.wireOp",EDGE,"E72.1");var subQ16=sQuery(id+"F12.wireOp",EDGE,"E74.1");var subQ18=sQuery(id+"F12.wireOp",EDGE,"E74.8");Q0=qUnion([makeQuery(id+"F12.imprint","IMPRINT",FACE,{"disambiguationData":[TD([[makeQuery(id+"F12.imprint","IMPRINT",EDGE,{"derivedFrom":subQ7}),1.0]])]}),makeQuery(id+"F12.imprint","IMPRINT",FACE,{"disambiguationData":[TD([[makeQuery(id+"F12.imprint","IMPRINT",EDGE,{"derivedFrom":subQ14}),1.0]])]}),makeQuery(id+"F12.imprint","IMPRINT",FACE,{"disambiguationData":[TD([[makeQuery(id+"F12.imprint","IMPRINT",EDGE,{"derivedFrom":subQ16}),1.0]])]}),makeQuery(id+"F12.imprint","IMPRINT",FACE,{"disambiguationData":[TD([[makeQuery(id+"F12.imprint","IMPRINT",EDGE,{"derivedFrom":subQ18}),-1.0]])]})]);}
            var Q1;
            Q1=makeQuery(id+"F5.boolean.opBoolean","SPLIT",FACE,{"disambiguationData":[TD([makeQuery(id+"F5.opExtrude","SWEPT_FACE",FACE,{"disambiguationData":[OSD([sQuery(id+"F4.wireOp",EDGE,"E41")])]})])],"derivedFrom":makeQuery(id+"F3.boolean.opBoolean","COPY",FACE,{"derivedFrom":makeQuery(id+"F3.opExtrude","CAP_FACE",FACE,{"disambiguationData":[OSD([sQuery(id+"F0.wireOp",EDGE,"E25.0"),sQuery(id+"F0.wireOp",EDGE,"E25.1"),sQuery(id+"F0.wireOp",EDGE,"E25.2"),sQuery(id+"F0.wireOp",EDGE,"E25.3"),sQuery(id+"F0.wireOp",EDGE,"E25.4"),sQuery(id+"F0.wireOp",EDGE,"E25.5"),sQuery(id+"F0.wireOp",EDGE,"E25.6"),sQuery(id+"F0.wireOp",EDGE,"E25.7")])],"isStart":false})})});
            extrude(context, id + "F13", {"entities" : qUnion([Q0]), "operationType" : NewBodyOperationType.REMOVE, "endBound" : BoundingType.UP_TO_SURFACE, "endBoundEntityFace" : qUnion([Q1]), "depth" : 25 * mm});
        }
        {
            var Q0;
            Q0=makeQuery(id+"F3.boolean.opBoolean","COPY",EDGE,{"derivedFrom":makeQuery(id+"F3.opExtrude","CAP_EDGE",EDGE,{"disambiguationData":[OSD([sQuery(id+"F0.wireOp",EDGE,"E25.6")])],"isStart":false})});
            var Q1;
            Q1=makeQuery(id+"F8.boolean.opBoolean","INTERSECT",EDGE,{"derivedFrom":[makeQuery(id+"F5.opExtrude","SWEPT_FACE",FACE,{"disambiguationData":[OSD([sQuery(id+"F4.wireOp",EDGE,"E30")])]}),makeQuery(id+"F8.opExtrude","CAP_FACE",FACE,{"disambiguationData":[OSD([sQuery(id+"F7.wireOp",EDGE,"E67")])],"isStart":false})]});
            var Q2;
            Q2=makeQuery(id+"F8.boolean.opBoolean","INTERSECT",EDGE,{"disambiguationData":[OD(1.0)],"derivedFrom":[makeQuery(id+"F5.opExtrude","SWEPT_FACE",FACE,{"disambiguationData":[OSD([sQuery(id+"F4.wireOp",EDGE,"E30")])]}),makeQuery(id+"F8.opExtrude","SWEPT_FACE",FACE,{"disambiguationData":[OSD([sQuery(id+"F7.wireOp",EDGE,"E67")])]})]});
            var Q3;
            {var subQ0=sQuery(id+"F4.wireOp",EDGE,"E30");Q3=makeQuery(id+"F8.boolean.opBoolean","SPLIT",EDGE,{"disambiguationData":[TD([makeQuery(id+"F5.opExtrude","SWEPT_FACE",FACE,{"disambiguationData":[OSD([sQuery(id+"F4.wireOp",EDGE,"E35.filletArc")])]})])],"derivedFrom":makeQuery(id+"F5.opExtrude","CAP_EDGE",EDGE,{"disambiguationData":[OSD([subQ0])],"isStart":false})});}
            var Q4;
            {var subQ0=sQuery(id+"F0.wireOp",EDGE,"E25.7");var subQ1=sQuery(id+"F0.wireOp",EDGE,"E25.1");var subQ2=sQuery(id+"F0.wireOp",EDGE,"E25.6");var subQ3=sQuery(id+"F0.wireOp",EDGE,"E25.5");var subQ4=sQuery(id+"F0.wireOp",EDGE,"E25.4");var subQ5=sQuery(id+"F0.wireOp",EDGE,"E25.0");var subQ6=sQuery(id+"F0.wireOp",EDGE,"E25.2");var subQ7=sQuery(id+"F0.wireOp",EDGE,"E25.3");Q4=makeQuery(id+"F8.boolean.opBoolean","INTERSECT",EDGE,{"derivedFrom":[makeQuery(id+"F5.boolean.opBoolean","SPLIT",FACE,{"disambiguationData":[TD([makeQuery(id+"F2.opExtrude","SWEPT_FACE",FACE,{"disambiguationData":[OSD([subQ5])]})])],"derivedFrom":makeQuery(id+"F3.boolean.opBoolean","COPY",FACE,{"derivedFrom":makeQuery(id+"F3.opExtrude","CAP_FACE",FACE,{"disambiguationData":[OSD([subQ5,subQ1,subQ6,subQ7,subQ4,subQ3,subQ2,subQ0])],"isStart":false})})}),makeQuery(id+"F8.opExtrude","SWEPT_FACE",FACE,{"disambiguationData":[OSD([sQuery(id+"F7.wireOp",EDGE,"E67")])]})]});}
            var Q5;
            Q5=makeQuery(id+"F8.boolean.opBoolean","INTERSECT",EDGE,{"disambiguationData":[OD(0.0)],"derivedFrom":[makeQuery(id+"F5.opExtrude","SWEPT_FACE",FACE,{"disambiguationData":[OSD([sQuery(id+"F4.wireOp",EDGE,"E30")])]}),makeQuery(id+"F8.opExtrude","SWEPT_FACE",FACE,{"disambiguationData":[OSD([sQuery(id+"F7.wireOp",EDGE,"E67")])]})]});
            fillet(context, id + "F14", {"entities" : qUnion([Q0, Q1, Q2, Q3, Q4, Q5]), "radius" : 3 * mm, "tangentPropagation" : true, "allowEdgeOverflow" : false});
        }
        {
            var Q0;
            Q0=makeQuery(id+"F1.opExtrude","CAP_EDGE",EDGE,{"disambiguationData":[OSD([sQuery(id+"F0.wireOp",EDGE,"E1.bottom")])],"isStart":false});
            fillet(context, id + "F15", {"entities" : qUnion([Q0]), "radius" : 2 * mm, "tangentPropagation" : true, "allowEdgeOverflow" : false});
        }
        {
            var Q0;
            {var subQ0=sQuery(id+"F0.wireOp",EDGE,"E21.filletArc");var subQ1=sQuery(id+"F0.wireOp",EDGE,"E7");var subQ2=sQuery(id+"F0.wireOp",EDGE,"E6");var subQ3=sQuery(id+"F0.wireOp",EDGE,"E5");var subQ4=sQuery(id+"F0.wireOp",EDGE,"E4");var subQ5=sQuery(id+"F0.wireOp",EDGE,"E22.filletArc");var subQ6=sQuery(id+"F0.wireOp",EDGE,"E1.bottom");var subQ7=sQuery(id+"F0.wireOp",EDGE,"E1.right");var subQ8=sQuery(id+"F0.wireOp",EDGE,"E1.top");var subQ9=sQuery(id+"F0.wireOp",EDGE,"E1.left");var subQ10=sQuery(id+"F0.wireOp",EDGE,"E23.filletArc");var subQ11=sQuery(id+"F0.wireOp",EDGE,"E24.filletArc");Q0=makeQuery(id+"F2.boolean.opBoolean","SPLIT",FACE,{"disambiguationData":[TD([makeQuery(id+"F1.opExtrude","SWEPT_FACE",FACE,{"disambiguationData":[OSD([subQ6])]})])],"derivedFrom":makeQuery(id+"F1.opExtrude","CAP_FACE",FACE,{"disambiguationData":[OSD([subQ6,subQ8,subQ9,subQ7,subQ4,subQ3,subQ2,subQ1,subQ0,subQ5,subQ10,subQ11])],"isStart":true})});}
            var sketch = newSketch(context, id + "F16", { "sketchPlane" : qUnion([Q0])});
            skLineSegment(sketch, "E79.0", {"start": v(-70, 90) * mm, "end": v(70, 90) * mm});
            skArc(sketch, "E79.1", {"start": v(-70, 90) * mm, "mid": v(-77.07, 87.07) * mm, "end": v(-80, 80) * mm});
            skLineSegment(sketch, "E79.2", {"start": v(-80, -80) * mm, "end": v(-80, 80) * mm});
            skArc(sketch, "E79.3", {"start": v(-80, -80) * mm, "mid": v(-77.07, -87.07) * mm, "end": v(-70, -90) * mm});
            skLineSegment(sketch, "E79.4", {"start": v(-70, -90) * mm, "end": v(70, -90) * mm});
            skArc(sketch, "E79.5", {"start": v(70, -90) * mm, "mid": v(77.07, -87.07) * mm, "end": v(80, -80) * mm});
            skLineSegment(sketch, "E79.6", {"start": v(80, -80) * mm, "end": v(80, 80) * mm});
            skArc(sketch, "E79.7", {"start": v(80, 80) * mm, "mid": v(77.07, 87.07) * mm, "end": v(70, 90) * mm});
            skCircle(sketch, "E79.8", {"center": v(60, 67.5) * mm, "radius": 4 * mm});
            skCircle(sketch, "E79.9", {"center": v(60, -67.5) * mm, "radius": 4 * mm});
            skCircle(sketch, "E79.10", {"center": v(-60, -67.5) * mm, "radius": 4 * mm});
            skCircle(sketch, "E79.11", {"center": v(-60, 67.5) * mm, "radius": 4 * mm});
            skArc(sketch, "E79.12", {"start": v(56.15, 48.18) * mm, "mid": v(0, 67.5) * mm, "end": v(-56.15, 48.18) * mm});
            skLineSegment(sketch, "E79.13", {"start": v(-60, 40.3) * mm, "end": v(-60, -40.3) * mm});
            skArc(sketch, "E79.14", {"start": v(-56.15, -48.18) * mm, "mid": v(0, -67.5) * mm, "end": v(56.15, -48.18) * mm});
            skArc(sketch, "E79.15", {"start": v(-60, -40.3) * mm, "mid": v(-58.99, -44.68) * mm, "end": v(-56.15, -48.18) * mm});
            skArc(sketch, "E79.16", {"start": v(-56.15, 48.18) * mm, "mid": v(-58.99, 44.68) * mm, "end": v(-60, 40.3) * mm});
            skArc(sketch, "E79.17", {"start": v(60, 40.3) * mm, "mid": v(58.99, 44.68) * mm, "end": v(56.15, 48.18) * mm});
            skLineSegment(sketch, "E79.18", {"start": v(60, 40.3) * mm, "end": v(60, -40.3) * mm});
            skArc(sketch, "E79.19", {"start": v(56.15, -48.18) * mm, "mid": v(58.99, -44.68) * mm, "end": v(60, -40.3) * mm});
            skLineSegment(sketch, "E80", {"start": v(0, 90) * mm, "end": v(0, 120) * mm, "construction": true});
            skCircle(sketch, "E81", {"center": v(0, 120) * mm, "radius": 6 * mm});
            skLineSegment(sketch, "E82", {"start": v(-33, 90) * mm, "end": v(-15, 108) * mm});
            skLineSegment(sketch, "E83", {"start": v(-15, 108) * mm, "end": v(-15, 120) * mm});
            skLineSegment(sketch, "E84", {"start": v(33, 90) * mm, "end": v(15, 108) * mm});
            skLineSegment(sketch, "E85", {"start": v(15, 108) * mm, "end": v(15, 120) * mm});
            skArc(sketch, "E86", {"start": v(15, 120) * mm, "mid": v(0, 135) * mm, "end": v(-15, 120) * mm});
            skLineSegment(sketch, "E87", {"start": v(-80, 0) * mm, "end": v(80, 0) * mm, "construction": true});
            skLineSegment(sketch, "E88.MirrorCS", {"start": v(33, -90) * mm, "end": v(15, -108) * mm});
            skLineSegment(sketch, "E89.MirrorCS", {"start": v(0, -90) * mm, "end": v(0, -120) * mm, "construction": true});
            skLineSegment(sketch, "E90.MirrorCS", {"start": v(-33, -90) * mm, "end": v(-15, -108) * mm});
            skArc(sketch, "E91.MirrorCS", {"start": v(15, -120) * mm, "mid": v(0, -135) * mm, "end": v(-15, -120) * mm});
            skLineSegment(sketch, "E92.MirrorCS", {"start": v(15, -108) * mm, "end": v(15, -120) * mm});
            skCircle(sketch, "E93.MirrorC", {"center": v(0, -120) * mm, "radius": 6 * mm});
            skLineSegment(sketch, "E94.MirrorCS", {"start": v(-15, -108) * mm, "end": v(-15, -120) * mm});
            skSolve(sketch);
        }
        {
            var Q0;
            {var subQ1=sQuery(id+"F16.wireOp",EDGE,"E88.MirrorCS");Q0=makeQuery(id+"F16.imprint","IMPRINT",FACE,{"disambiguationData":[TD([[makeQuery(id+"F16.imprint","IMPRINT",EDGE,{"derivedFrom":subQ1}),-1.0]])]});}
            var Q1;
            Q1=makeQuery(id+"F16.imprint","IMPRINT",FACE,{"disambiguationData":[TD([[makeQuery(id+"F16.imprint","IMPRINT",EDGE,{"derivedFrom":sQuery(id+"F16.wireOp",EDGE,"E81")}),-1.0]])]});
            var Q2;
            {var subQ1=sQuery(id+"F16.wireOp",EDGE,"E79.1");Q2=makeQuery(id+"F16.imprint","IMPRINT",FACE,{"disambiguationData":[TD([[makeQuery(id+"F16.imprint","IMPRINT",EDGE,{"derivedFrom":subQ1}),1.0]])]});}
            var Q3;
            Q3=makeQuery(id+"F2.opExtrude","CAP_FACE",FACE,{"disambiguationData":[OSD([sQuery(id+"F0.wireOp",EDGE,"E12"),sQuery(id+"F0.wireOp",EDGE,"E13"),sQuery(id+"F0.wireOp",EDGE,"E14"),sQuery(id+"F0.wireOp",EDGE,"E15"),sQuery(id+"F0.wireOp",EDGE,"E17.filletArc"),sQuery(id+"F0.wireOp",EDGE,"E18.filletArc"),sQuery(id+"F0.wireOp",EDGE,"E19.filletArc"),sQuery(id+"F0.wireOp",EDGE,"E20.filletArc"),sQuery(id+"F0.wireOp",EDGE,"E25.0"),sQuery(id+"F0.wireOp",EDGE,"E25.1"),sQuery(id+"F0.wireOp",EDGE,"E25.2"),sQuery(id+"F0.wireOp",EDGE,"E25.3"),sQuery(id+"F0.wireOp",EDGE,"E25.4"),sQuery(id+"F0.wireOp",EDGE,"E25.5"),sQuery(id+"F0.wireOp",EDGE,"E25.6"),sQuery(id+"F0.wireOp",EDGE,"E25.7")])],"isStart":false});
            extrude(context, id + "F17", {"entities" : qUnion([Q0, Q1, Q2]), "endBound" : BoundingType.UP_TO_SURFACE, "endBoundEntityFace" : qUnion([Q3]), "depth" : 25 * mm});
        }
    });
